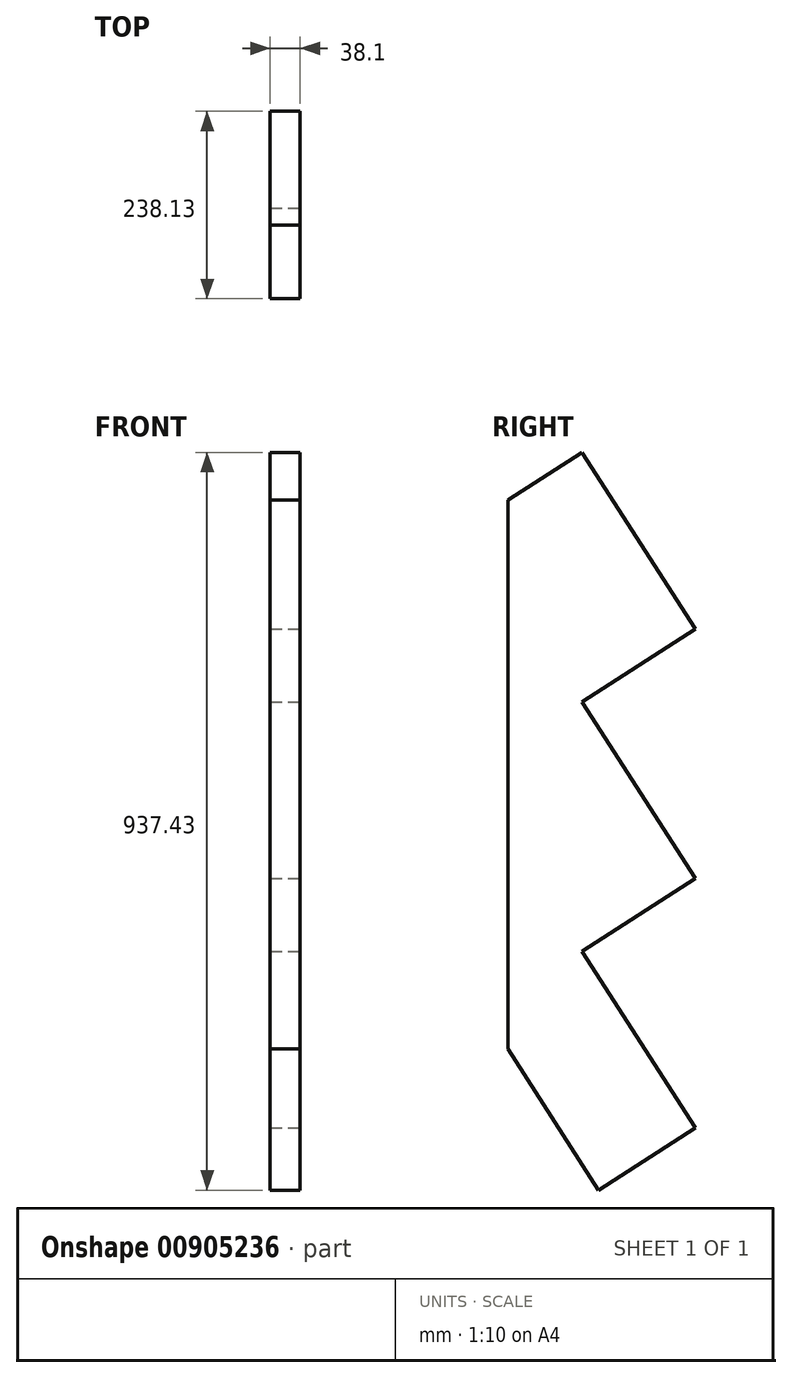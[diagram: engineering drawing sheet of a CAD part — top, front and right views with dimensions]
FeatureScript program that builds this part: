
annotation { "Feature Type Name" : "Feature", "Feature Type Description" : "" }
export const myFeature = defineFeature(function(context is Context, id is Id, definition is map)
    precondition{}
    {
        {
            var Q0;
            Q0=qCreatedBy(makeId("Top.planeOp"),FACE);
            var sketch = newSketch(context, id + "F0", { "sketchPlane" : qUnion([Q0])});
            skLineSegment(sketch, "E0.bottom", {"start": v(0, 238.13) * mm, "end": v(38.1, 238.13) * mm});
            skLineSegment(sketch, "E0.top", {"start": v(0, 0) * mm, "end": v(38.1, 0) * mm});
            skLineSegment(sketch, "E0.left", {"start": v(0, 238.13) * mm, "end": v(0, 0) * mm});
            skLineSegment(sketch, "E0.right", {"start": v(38.1, 238.13) * mm, "end": v(38.1, 0) * mm});
            skSolve(sketch);
        }
        {
            var Q0;
            Q0 = qSketchRegion(id + "F0", true);
            extrude(context, id + "F1", {"entities" : qUnion([Q0]), "depth" : 990.6 * mm, "offsetDistance" : 25.4 * mm});
        }
        {
            var Q0;
            Q0=makeQuery(id+"F1.opExtrude","SWEPT_FACE",FACE,{"disambiguationData":[OSD([sQuery(id+"F0.wireOp",EDGE,"E0.right")])]});
            var sketch = newSketch(context, id + "F2", { "sketchPlane" : qUnion([Q0])});
            skLineSegment(sketch, "E1", {"start": v(0, 179.31) * mm, "end": v(115.27, 0) * mm});
            skLineSegment(sketch, "E2", {"start": v(115.27, 0) * mm, "end": v(238.12, 78.98) * mm});
            skLineSegment(sketch, "E3", {"start": v(238.13, 78.98) * mm, "end": v(93.9, 303.32) * mm});
            skLineSegment(sketch, "E4", {"start": v(93.9, 303.32) * mm, "end": v(238.12, 396.03) * mm});
            skLineSegment(sketch, "E5", {"start": v(238.12, 396.03) * mm, "end": v(93.9, 620.38) * mm});
            skLineSegment(sketch, "E6", {"start": v(93.9, 620.38) * mm, "end": v(238.13, 713.09) * mm});
            skLineSegment(sketch, "E7", {"start": v(238.13, 713.09) * mm, "end": v(93.9, 937.43) * mm});
            skLineSegment(sketch, "E8", {"start": v(93.9, 937.43) * mm, "end": v(-444.02, 591.62) * mm});
            skLineSegment(sketch, "E9", {"start": v(-444.02, 591.62) * mm, "end": v(-444.02, 1649.13) * mm});
            skLineSegment(sketch, "E10", {"start": v(-444.02, 1649.13) * mm, "end": v(438.82, 1649.13) * mm});
            skLineSegment(sketch, "E11", {"start": v(438.82, 1649.13) * mm, "end": v(438.82, -479.18) * mm});
            skLineSegment(sketch, "E12", {"start": v(438.82, -479.18) * mm, "end": v(-215.23, -479.18) * mm});
            skLineSegment(sketch, "E13", {"start": v(-215.23, -479.18) * mm, "end": v(-215.23, 179.31) * mm});
            skLineSegment(sketch, "E14", {"start": v(-215.23, 179.31) * mm, "end": v(0, 179.31) * mm});
            skLineSegment(sketch, "E15", {"start": v(269.1, 1028.92) * mm, "end": v(247.74, 1015.19) * mm, "construction": true});
            skLineSegment(sketch, "E16", {"start": v(247.74, 1015.19) * mm, "end": v(217.52, 1062.2) * mm, "construction": true});
            skLineSegment(sketch, "E17", {"start": v(217.52, 1062.2) * mm, "end": v(73.3, 969.48) * mm, "construction": true});
            skLineSegment(sketch, "E18", {"start": v(93.9, 937.43) * mm, "end": v(166.72, 984.24) * mm, "construction": true});
            skLineSegment(sketch, "E19", {"start": v(93.9, 937.43) * mm, "end": v(73.3, 969.48) * mm, "construction": true});
            skLineSegment(sketch, "E20", {"start": v(166.72, 984.24) * mm, "end": v(146.12, 1016.29) * mm, "construction": true});
            skLineSegment(sketch, "E21", {"start": v(-157.34, 1692.28) * mm, "end": v(269.1, 1028.92) * mm, "construction": true});
            skPoint(sketch, "E22", {"position": v(119.06, 0) * mm});
            skLineSegment(sketch, "E23", {"start": v(268.08, 713.47) * mm, "end": v(115.27, 951.17) * mm, "construction": true});
            skLineSegment(sketch, "E24", {"start": v(249.78, 424.88) * mm, "end": v(115.27, 634.11) * mm, "construction": true});
            skLineSegment(sketch, "E25", {"start": v(263.85, 85.93) * mm, "end": v(115.27, 317.06) * mm, "construction": true});
            skLineSegment(sketch, "E26", {"start": v(268.08, 1231.65) * mm, "end": v(268.08, 713.47) * mm});
            skSolve(sketch);
        }
        {
            var Q0;
            Q0 = qSketchRegion(id + "F2", true);
            extrude(context, id + "F3", {"entities" : qUnion([Q0]), "operationType" : NewBodyOperationType.REMOVE, "endBound" : BoundingType.THROUGH_ALL, "oppositeDirection" : true, "depth" : 25.4 * mm, "offsetDistance" : 25.4 * mm});
        }
    });
